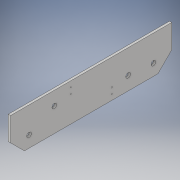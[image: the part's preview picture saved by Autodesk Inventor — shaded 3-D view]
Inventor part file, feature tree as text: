
AUTODESK INVENTOR PART (.ipt)
format: ipt  version: 2017 (Build 210142000, 142)  size: 154,624 bytes
history: native  units: in
note: dims shown in document units (in); Inventor stores cm internally (conversion verified against a paired STEP export)
features: extrude x3, sketch x3, chamfer x2, projected_geometry x2
ambient origin geometry x8: Origin, YZ Plane, XZ Plane, XY Plane, X Axis, Y Axis, Z Axis, Center Point
bodies: Solid1 (feature_tree)
feature tree (10):
  extrude  "Extrusion1"  Depth=17.5in
  chamfer  "Chamfer1"  Distance=2.0in
  chamfer  "Chamfer2"  Distance=2.0in
  extrude  "Extrusion2"  Depth=0.25in TaperAngle=0.0deg
  extrude  "Extrusion3"  Depth=0.25in TaperAngle=45.0deg
  sketch  "Sketch1"  dims[d0=4.07in d1=17.5in]
  sketch  "Sketch2"  dims[d2=0.501in]
  projected_geometry  "Projected Loop1"
  sketch  "Sketch3"  dims[d3=1.25in d4=2.0in d5=2.0in d6=0.25in d7=0.0in d8=1.5in d9=0.125in d10=45.0deg d11=1.5in d12=0.125in d13=45.0deg d14=0.501in d15=4.741in d16=1.469in d17=0.501in d18=1.469in d19=4.741in d20=1.0in d21=0.0in d22=6.517in d23=0.125in d24=0.603in d25=0.125in d26=0.63in d27=6.517in d28=0.125in d29=0.603in d30=6.517in d31=0.125in d32=0.63in d33=6.517in d34=0.125in d35=6.517in d36=0.603in d37=0.125in d38=0.63in d39=0.125in d40=0.125in d41=0.603in d42=0.63in d43=6.517in d44=1.0in d45=0.0in]
  projected_geometry  "Projected Loop2"
